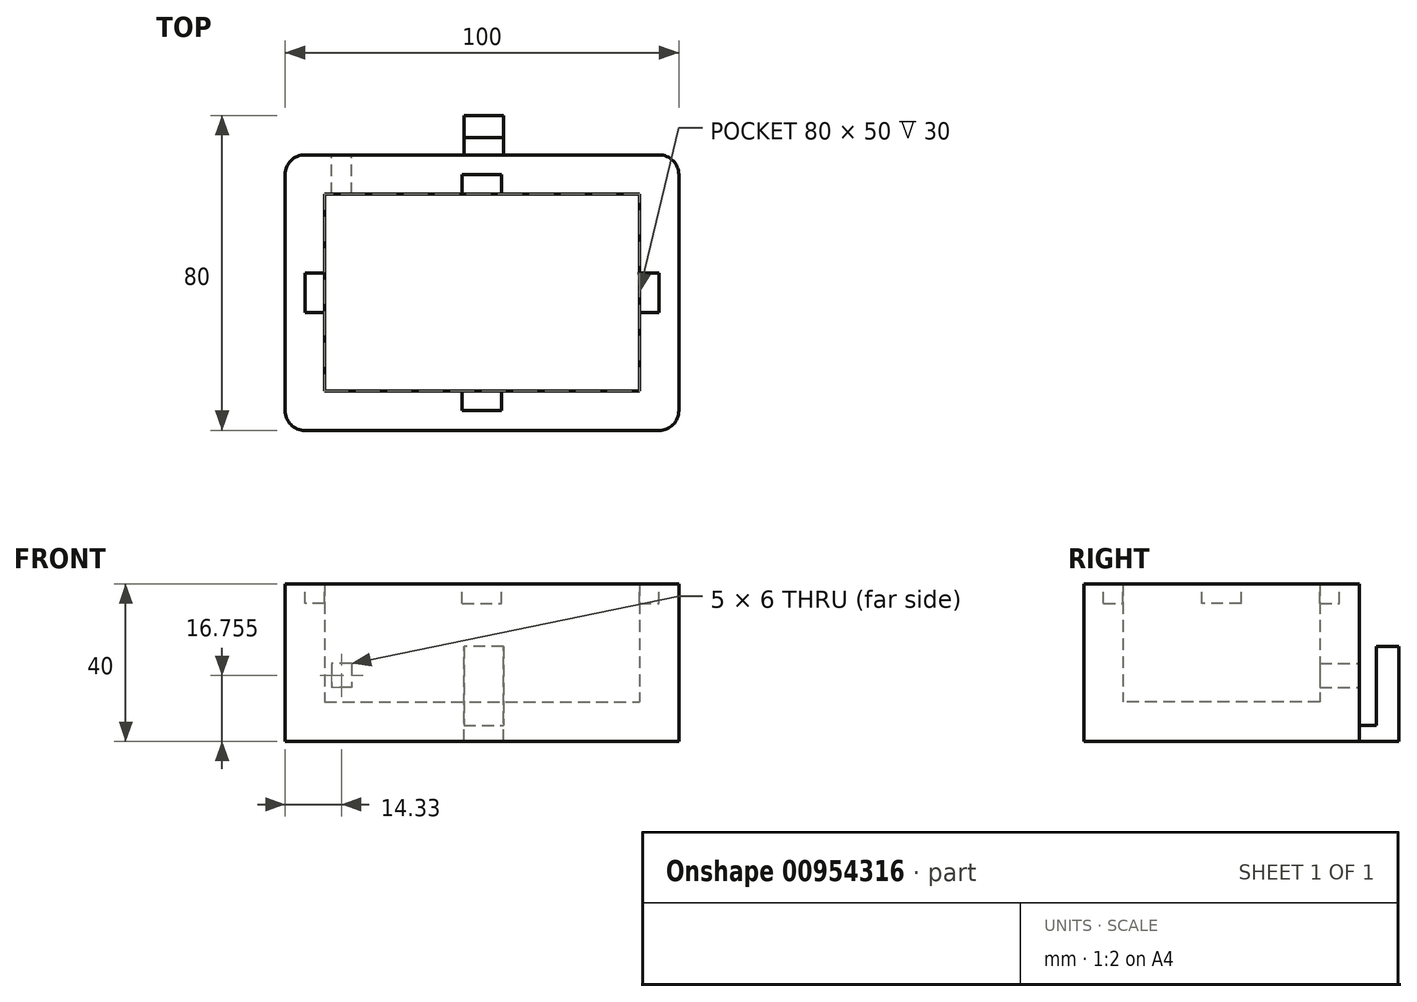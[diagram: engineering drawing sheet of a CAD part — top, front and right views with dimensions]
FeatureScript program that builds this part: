
annotation { "Feature Type Name" : "Feature", "Feature Type Description" : "" }
export const myFeature = defineFeature(function(context is Context, id is Id, definition is map)
    precondition{}
    {
        {
            var Q0;
            Q0=qCreatedBy(makeId("Top.planeOp"),FACE);
            var sketch = newSketch(context, id + "F0", { "sketchPlane" : qUnion([Q0])});
            skLineSegment(sketch, "E0.bottom", {"start": v(-45, 35) * mm, "end": v(45, 35) * mm});
            skLineSegment(sketch, "E0.top", {"start": v(-45, -35) * mm, "end": v(45, -35) * mm});
            skLineSegment(sketch, "E0.left", {"start": v(-50, 30) * mm, "end": v(-50, -30) * mm});
            skLineSegment(sketch, "E0.right", {"start": v(50, 30) * mm, "end": v(50, -30) * mm});
            skPoint(sketch, "E0.middle", {"position": v(0, 0) * mm});
            skPoint(sketch, "E1.visualSharp", {"position": v(-50, 35) * mm});
            skArc(sketch, "E1.filletArc", {"start": v(-45, 35) * mm, "mid": v(-48.54, 33.54) * mm, "end": v(-50, 30) * mm});
            skPoint(sketch, "E2.visualSharp", {"position": v(-50, -35) * mm});
            skArc(sketch, "E2.filletArc", {"start": v(-50, -30) * mm, "mid": v(-48.54, -33.54) * mm, "end": v(-45, -35) * mm});
            skPoint(sketch, "E3.visualSharp", {"position": v(50, 35) * mm});
            skArc(sketch, "E3.filletArc", {"start": v(50, 30) * mm, "mid": v(48.54, 33.54) * mm, "end": v(45, 35) * mm});
            skPoint(sketch, "E4.visualSharp", {"position": v(50, -35) * mm});
            skArc(sketch, "E4.filletArc", {"start": v(45, -35) * mm, "mid": v(48.54, -33.54) * mm, "end": v(50, -30) * mm});
            skSolve(sketch);
        }
        {
            var Q0;
            Q0=makeQuery(id+"F0.imprint","IMPRINT",FACE,{"disambiguationData":[TD([[makeQuery(id+"F0.imprint","IMPRINT",EDGE,{"derivedFrom":sQuery(id+"F0.wireOp",EDGE,"E0.bottom")}),-1.0]])]});
            extrude(context, id + "F1", {"entities" : qUnion([Q0]), "depth" : 40 * mm, "offsetDistance" : 25 * mm});
        }
        {
            var Q0;
            Q0=makeQuery(id+"F1.opExtrude","CAP_FACE",FACE,{"disambiguationData":[OSD([sQuery(id+"F0.wireOp",EDGE,"E0.bottom"),sQuery(id+"F0.wireOp",EDGE,"E0.top"),sQuery(id+"F0.wireOp",EDGE,"E0.left"),sQuery(id+"F0.wireOp",EDGE,"E0.right"),sQuery(id+"F0.wireOp",EDGE,"E1.filletArc"),sQuery(id+"F0.wireOp",EDGE,"E2.filletArc"),sQuery(id+"F0.wireOp",EDGE,"E3.filletArc"),sQuery(id+"F0.wireOp",EDGE,"E4.filletArc")])],"isStart":false});
            shell(context, id + "F2", {"entities" : qUnion([Q0]), "thickness" : 10 * mm});
        }
        {
            var Q0;
            Q0=makeQuery(id+"F1.opExtrude","SWEPT_FACE",FACE,{"disambiguationData":[OSD([sQuery(id+"F0.wireOp",EDGE,"E0.bottom")])]});
            var sketch = newSketch(context, id + "F3", { "sketchPlane" : qUnion([Q0])});
            skLineSegment(sketch, "E5.bottom", {"start": v(-5.42, 0) * mm, "end": v(4.58, 0) * mm});
            skLineSegment(sketch, "E5.top", {"start": v(-5.42, 4.06) * mm, "end": v(4.58, 4.06) * mm});
            skLineSegment(sketch, "E5.left", {"start": v(-5.42, 0) * mm, "end": v(-5.42, 4.06) * mm});
            skLineSegment(sketch, "E5.right", {"start": v(4.58, 0) * mm, "end": v(4.58, 4.06) * mm});
            skSolve(sketch);
        }
        {
            var Q0;
            Q0=makeQuery(id+"F3.imprint","IMPRINT",FACE,{"disambiguationData":[TD([[makeQuery(id+"F3.imprint","IMPRINT",EDGE,{"derivedFrom":sQuery(id+"F3.wireOp",EDGE,"E5.bottom")}),-1.0]])]});
            extrude(context, id + "F4", {"entities" : qUnion([Q0]), "depth" : 10 * mm, "offsetDistance" : 25 * mm});
        }
        {
            var Q0;
            Q0=makeQuery(id+"F4.opExtrude","SWEPT_FACE",FACE,{"disambiguationData":[OSD([sQuery(id+"F3.wireOp",EDGE,"E5.top")])]});
            var sketch = newSketch(context, id + "F5", { "sketchPlane" : qUnion([Q0])});
            skLineSegment(sketch, "E6.bottom", {"start": v(-4.58, 45) * mm, "end": v(5.42, 45) * mm});
            skLineSegment(sketch, "E6.top", {"start": v(-4.58, 39.37) * mm, "end": v(5.42, 39.37) * mm});
            skLineSegment(sketch, "E6.left", {"start": v(-4.58, 45) * mm, "end": v(-4.58, 39.37) * mm});
            skLineSegment(sketch, "E6.right", {"start": v(5.42, 45) * mm, "end": v(5.42, 39.37) * mm});
            skSolve(sketch);
        }
        {
            var Q0;
            Q0=makeQuery(id+"F5.imprint","IMPRINT",FACE,{"disambiguationData":[TD([[makeQuery(id+"F5.imprint","IMPRINT",EDGE,{"derivedFrom":sQuery(id+"F5.wireOp",EDGE,"E6.bottom")}),1.0]])]});
            extrude(context, id + "F6", {"entities" : qUnion([Q0]), "operationType" : NewBodyOperationType.ADD, "depth" : 20 * mm, "offsetDistance" : 25 * mm});
        }
        {
            var Q0;
            Q0=makeQuery(id+"F1.opExtrude","CAP_FACE",FACE,{"disambiguationData":[OSD([sQuery(id+"F0.wireOp",EDGE,"E0.bottom"),sQuery(id+"F0.wireOp",EDGE,"E0.top"),sQuery(id+"F0.wireOp",EDGE,"E0.left"),sQuery(id+"F0.wireOp",EDGE,"E0.right"),sQuery(id+"F0.wireOp",EDGE,"E1.filletArc"),sQuery(id+"F0.wireOp",EDGE,"E2.filletArc"),sQuery(id+"F0.wireOp",EDGE,"E3.filletArc"),sQuery(id+"F0.wireOp",EDGE,"E4.filletArc")])],"isStart":false});
            var sketch = newSketch(context, id + "F7", { "sketchPlane" : qUnion([Q0])});
            skLineSegment(sketch, "E7", {"start": v(5, 25) * mm, "end": v(5, 30) * mm});
            skLineSegment(sketch, "E8", {"start": v(5, 30) * mm, "end": v(-5, 30) * mm});
            skLineSegment(sketch, "E9", {"start": v(-5, 30) * mm, "end": v(-5, 25) * mm});
            skLineSegment(sketch, "E10", {"start": v(-5, 25) * mm, "end": v(5, 25) * mm});
            skLineSegment(sketch, "E11.MirrorCS", {"start": v(5, -30) * mm, "end": v(-5, -30) * mm});
            skLineSegment(sketch, "E12.MirrorCS", {"start": v(-5, -30) * mm, "end": v(-5, -25) * mm});
            skLineSegment(sketch, "E13.MirrorCS", {"start": v(-5, -25) * mm, "end": v(5, -25) * mm});
            skLineSegment(sketch, "E14.MirrorCS", {"start": v(5, -25) * mm, "end": v(5, -30) * mm});
            skLineSegment(sketch, "E15", {"start": v(-40, 5) * mm, "end": v(-45, 5) * mm});
            skLineSegment(sketch, "E16", {"start": v(-45, 5) * mm, "end": v(-45, -5) * mm});
            skLineSegment(sketch, "E17", {"start": v(-45, -5) * mm, "end": v(-40, -5) * mm});
            skLineSegment(sketch, "E18", {"start": v(-40, -5) * mm, "end": v(-40, 5) * mm});
            skLineSegment(sketch, "E19.MirrorCS", {"start": v(40, 5) * mm, "end": v(45, 5) * mm});
            skLineSegment(sketch, "E20.MirrorCS", {"start": v(40, -5) * mm, "end": v(40, 5) * mm});
            skLineSegment(sketch, "E21.MirrorCS", {"start": v(45, -5) * mm, "end": v(40, -5) * mm});
            skLineSegment(sketch, "E22.MirrorCS", {"start": v(45, 5) * mm, "end": v(45, -5) * mm});
            skSolve(sketch);
        }
        {
            var Q0;
            Q0=makeQuery(id+"F7.imprint","IMPRINT",FACE,{"disambiguationData":[TD([[makeQuery(id+"F7.imprint","IMPRINT",EDGE,{"derivedFrom":sQuery(id+"F7.wireOp",EDGE,"E7")}),1.0]])]});
            var Q1;
            Q1=makeQuery(id+"F7.imprint","IMPRINT",FACE,{"disambiguationData":[TD([[makeQuery(id+"F7.imprint","IMPRINT",EDGE,{"derivedFrom":sQuery(id+"F7.wireOp",EDGE,"E15")}),1.0]])]});
            var Q2;
            Q2=makeQuery(id+"F7.imprint","IMPRINT",FACE,{"disambiguationData":[TD([[makeQuery(id+"F7.imprint","IMPRINT",EDGE,{"derivedFrom":sQuery(id+"F7.wireOp",EDGE,"E19.MirrorCS")}),-1.0]])]});
            var Q3;
            Q3=makeQuery(id+"F7.imprint","IMPRINT",FACE,{"disambiguationData":[TD([[makeQuery(id+"F7.imprint","IMPRINT",EDGE,{"derivedFrom":sQuery(id+"F7.wireOp",EDGE,"E11.MirrorCS")}),-1.0]])]});
            extrude(context, id + "F8", {"entities" : qUnion([Q0, Q1, Q2, Q3]), "operationType" : NewBodyOperationType.REMOVE, "oppositeDirection" : true, "depth" : 5 * mm, "offsetDistance" : 25 * mm});
        }
        {
            var Q0;
            Q0=makeQuery(id+"F1.opExtrude","SWEPT_FACE",FACE,{"disambiguationData":[OSD([sQuery(id+"F0.wireOp",EDGE,"E0.bottom")])]});
            var sketch = newSketch(context, id + "F9", { "sketchPlane" : qUnion([Q0])});
            skLineSegment(sketch, "E23.bottom", {"start": v(33.17, 19.76) * mm, "end": v(38.17, 19.76) * mm});
            skLineSegment(sketch, "E23.top", {"start": v(33.17, 13.76) * mm, "end": v(38.17, 13.76) * mm});
            skLineSegment(sketch, "E23.left", {"start": v(33.17, 19.76) * mm, "end": v(33.17, 13.76) * mm});
            skLineSegment(sketch, "E23.right", {"start": v(38.17, 19.76) * mm, "end": v(38.17, 13.76) * mm});
            skSolve(sketch);
        }
        {
            var Q0;
            Q0=makeQuery(id+"F9.imprint","IMPRINT",FACE,{"disambiguationData":[TD([[makeQuery(id+"F9.imprint","IMPRINT",EDGE,{"derivedFrom":sQuery(id+"F9.wireOp",EDGE,"E23.bottom")}),-1.0]])]});
            extrude(context, id + "F10", {"entities" : qUnion([Q0]), "operationType" : NewBodyOperationType.REMOVE, "oppositeDirection" : true, "depth" : 10 * mm, "offsetDistance" : 25 * mm});
        }
    });
